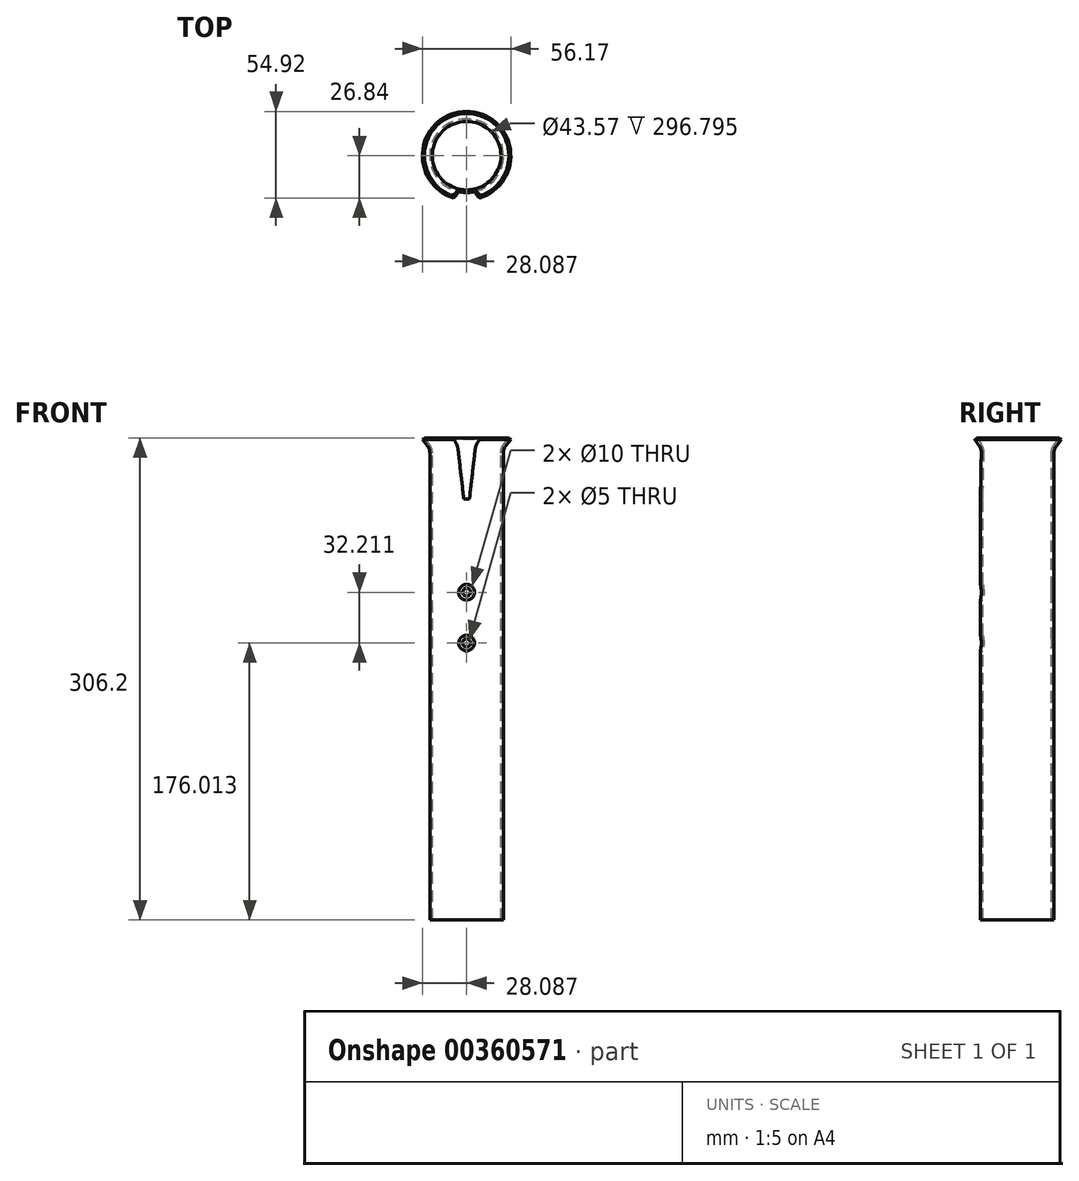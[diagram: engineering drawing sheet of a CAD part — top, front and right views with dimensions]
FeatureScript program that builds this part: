
annotation { "Feature Type Name" : "Feature", "Feature Type Description" : "" }
export const myFeature = defineFeature(function(context is Context, id is Id, definition is map)
    precondition{}
    {
        {
            var Q0;
            Q0=qCreatedBy(makeId("Front.planeOp"),FACE);
            var sketch = newSketch(context, id + "F0", { "sketchPlane" : qUnion([Q0])});
            skLineSegment(sketch, "E0.0", {"start": v(-35.58, 123.54) * mm, "end": v(-35.58, -173.26) * mm});
            skLineSegment(sketch, "E1", {"start": v(-35.58, -173.26) * mm, "end": v(-33.98, -173.26) * mm});
            skLineSegment(sketch, "E2", {"start": v(-57.36, 218.9) * mm, "end": v(-57.36, 39.96) * mm, "construction": true});
            skLineSegment(sketch, "E3", {"start": v(-35.58, 15.7) * mm, "end": v(-33.16, 15.7) * mm, "construction": true});
            skLineSegment(sketch, "E4", {"start": v(-33.55, 129.22) * mm, "end": v(-30.52, 132.94) * mm});
            skPoint(sketch, "E5.visualSharp", {"position": v(-35.58, 126.74) * mm});
            skArc(sketch, "E5.filletArc", {"start": v(-33.55, 129.22) * mm, "mid": v(-35.05, 126.55) * mm, "end": v(-35.58, 123.54) * mm});
            skLineSegment(sketch, "E6.0", {"start": v(-32.31, 128.21) * mm, "end": v(-29.28, 131.93) * mm});
            skArc(sketch, "E6.1", {"start": v(-32.31, 128.21) * mm, "mid": v(-33.55, 126.02) * mm, "end": v(-33.98, 123.54) * mm});
            skLineSegment(sketch, "E6.2", {"start": v(-33.98, 123.54) * mm, "end": v(-33.98, -173.26) * mm});
            skLineSegment(sketch, "E7", {"start": v(-30.52, 132.94) * mm, "end": v(-29.28, 131.93) * mm});
            skLineSegment(sketch, "E8", {"start": v(-55.5, 94.87) * mm, "end": v(-51.98, 125.42) * mm});
            skLineSegment(sketch, "E9", {"start": v(-48.74, 132.34) * mm, "end": v(-47, 134.15) * mm});
            skPoint(sketch, "E10.visualSharp", {"position": v(-51.52, 129.43) * mm});
            skArc(sketch, "E10.filletArc", {"start": v(-48.74, 132.34) * mm, "mid": v(-50.92, 129.15) * mm, "end": v(-51.98, 125.42) * mm});
            skPoint(sketch, "E11.MirrorCS.end.orphan", {"position": v(-55.5, 128.78) * mm});
            skPoint(sketch, "E11.MirrorCS.start.orphan", {"position": v(-48.74, 132.34) * mm});
            skLineSegment(sketch, "E12.MirrorCS", {"start": v(-59.24, 94.87) * mm, "end": v(-62.75, 125.42) * mm});
            skPoint(sketch, "E13.MirrorP", {"position": v(-63.2, 129.43) * mm});
            skArc(sketch, "E14.MirrorCS", {"start": v(-66, 132.34) * mm, "mid": v(-63.8, 129.15) * mm, "end": v(-62.75, 125.42) * mm});
            skPoint(sketch, "E15.MirrorP", {"position": v(-66, 132.34) * mm});
            skLineSegment(sketch, "E16.MirrorCS", {"start": v(-66, 132.34) * mm, "end": v(-67.72, 134.15) * mm});
            skLineSegment(sketch, "E17", {"start": v(-67.72, 134.15) * mm, "end": v(-47, 134.15) * mm});
            skLineSegment(sketch, "E18", {"start": v(-58.57, 94.27) * mm, "end": v(-56.16, 94.27) * mm});
            skPoint(sketch, "E19.visualSharp", {"position": v(-59.17, 94.27) * mm});
            skArc(sketch, "E19.filletArc", {"start": v(-59.24, 94.87) * mm, "mid": v(-59.02, 94.44) * mm, "end": v(-58.57, 94.27) * mm});
            skPoint(sketch, "E20.visualSharp", {"position": v(-55.56, 94.27) * mm});
            skArc(sketch, "E20.filletArc", {"start": v(-56.16, 94.27) * mm, "mid": v(-55.71, 94.44) * mm, "end": v(-55.5, 94.87) * mm});
            skCircle(sketch, "E21", {"center": v(-57.36, 34.96) * mm, "radius": 5 * mm});
            skCircle(sketch, "E22", {"center": v(-57.36, 2.75) * mm, "radius": 5 * mm});
            skCircle(sketch, "E23", {"center": v(-57.36, 34.96) * mm, "radius": 2.5 * mm});
            skCircle(sketch, "E24", {"center": v(-57.36, 2.75) * mm, "radius": 2.5 * mm});
            skLineSegment(sketch, "E25.trimOffspring", {"start": v(-57.36, 29.96) * mm, "end": v(-57.36, 7.75) * mm, "construction": true});
            skLineSegment(sketch, "E26.trimOffspring", {"start": v(-57.36, -2.25) * mm, "end": v(-57.36, -130.22) * mm, "construction": true});
            skSolve(sketch);
        }
        {
            var Q0;
            Q0=makeQuery(id+"F0.imprint","IMPRINT",FACE,{"disambiguationData":[TD([[makeQuery(id+"F0.imprint","IMPRINT",EDGE,{"derivedFrom":sQuery(id+"F0.wireOp",EDGE,"E8")}),1.0]])]});
            extrude(context, id + "F1", {"entities" : qUnion([Q0]), "depth" : 45 * mm});
        }
        {
            var Q0;
            Q0=makeQuery(id+"F0.imprint","IMPRINT",FACE,{"disambiguationData":[TD([[makeQuery(id+"F0.imprint","IMPRINT",EDGE,{"derivedFrom":sQuery(id+"F0.wireOp",EDGE,"E0.0")}),1.0]])]});
            var Q1;
            Q1=sQuery(id+"F0.wireOp",EDGE,"E2");
            revolve(context, id + "F2", {"operationType" : NewBodyOperationType.ADD, "entities" : qUnion([Q0]), "axis" : qUnion([Q1]), "revolveType" : RevolveType.FULL});
        }
        {
            var Q0;
            Q0=makeQuery(id+"F1.opExtrude","CAP_FACE",FACE,{"disambiguationData":[OSD([sQuery(id+"F0.wireOp",EDGE,"E8"),sQuery(id+"F0.wireOp",EDGE,"E9"),sQuery(id+"F0.wireOp",EDGE,"E10.filletArc"),sQuery(id+"F0.wireOp",EDGE,"E12.MirrorCS"),sQuery(id+"F0.wireOp",EDGE,"E14.MirrorCS"),sQuery(id+"F0.wireOp",EDGE,"E16.MirrorCS"),sQuery(id+"F0.wireOp",EDGE,"E17"),sQuery(id+"F0.wireOp",EDGE,"E18"),sQuery(id+"F0.wireOp",EDGE,"E19.filletArc"),sQuery(id+"F0.wireOp",EDGE,"E20.filletArc")])],"isStart":false});
            extrude(context, id + "F3", {"entities" : qUnion([Q0]), "operationType" : NewBodyOperationType.REMOVE, "oppositeDirection" : true, "depth" : 47.5 * mm});
        }
        {
            var Q0;
            Q0=makeQuery(id+"F0.imprint","IMPRINT",FACE,{"disambiguationData":[TD([[makeQuery(id+"F0.imprint","IMPRINT",EDGE,{"derivedFrom":sQuery(id+"F0.wireOp",EDGE,"E21")}),1.0]])]});
            extrude(context, id + "F4", {"entities" : qUnion([Q0]), "operationType" : NewBodyOperationType.REMOVE, "endBound" : BoundingType.THROUGH_ALL, "depth" : 37.2 * mm, "hasSecondDirection" : true, "secondDirectionOppositeDirection" : true, "secondDirectionDepth" : 10.2 * mm});
        }
        {
            var Q0;
            Q0=makeQuery(id+"F0.imprint","IMPRINT",FACE,{"disambiguationData":[TD([[makeQuery(id+"F0.imprint","IMPRINT",EDGE,{"derivedFrom":sQuery(id+"F0.wireOp",EDGE,"E22")}),1.0]])]});
            extrude(context, id + "F5", {"entities" : qUnion([Q0]), "operationType" : NewBodyOperationType.REMOVE, "endBound" : BoundingType.THROUGH_ALL, "depth" : 25 * mm, "hasSecondDirection" : true, "secondDirectionOppositeDirection" : true, "secondDirectionDepth" : 17.3 * mm});
        }
        {
            var Q0;
            Q0=makeQuery(id+"F0.imprint","IMPRINT",FACE,{"disambiguationData":[TD([[makeQuery(id+"F0.imprint","IMPRINT",EDGE,{"derivedFrom":sQuery(id+"F0.wireOp",EDGE,"E23")}),1.0]])]});
            extrude(context, id + "F6", {"entities" : qUnion([Q0]), "operationType" : NewBodyOperationType.REMOVE, "endBound" : BoundingType.THROUGH_ALL, "oppositeDirection" : true, "depth" : 28.4 * mm, "hasSecondDirection" : true, "secondDirectionOppositeDirection" : false, "secondDirectionDepth" : 25 * mm});
        }
        {
            var Q0;
            Q0=makeQuery(id+"F0.imprint","IMPRINT",FACE,{"disambiguationData":[TD([[makeQuery(id+"F0.imprint","IMPRINT",EDGE,{"derivedFrom":sQuery(id+"F0.wireOp",EDGE,"E24")}),1.0]])]});
            extrude(context, id + "F7", {"entities" : qUnion([Q0]), "operationType" : NewBodyOperationType.REMOVE, "depth" : 40.6 * mm, "hasSecondDirection" : true, "secondDirectionOppositeDirection" : true, "secondDirectionDepth" : 127.9 * mm});
        }
        {
            var Q0;
            Q0=makeQuery(id+"F0.imprint","IMPRINT",FACE,{"disambiguationData":[TD([[makeQuery(id+"F0.imprint","IMPRINT",EDGE,{"derivedFrom":sQuery(id+"F0.wireOp",EDGE,"E23")}),1.0]])]});
            extrude(context, id + "F8", {"entities" : qUnion([Q0]), "operationType" : NewBodyOperationType.REMOVE, "endBound" : BoundingType.THROUGH_ALL, "depth" : 25 * mm, "hasSecondDirection" : true, "secondDirectionOppositeDirection" : true, "secondDirectionDepth" : 25 * mm});
        }
    });
